# Revit family: RN 81167 Optipress-Aquaplus-Sicherheitsgarnitur
name_source: partatom
category: Rohrzubehör
units: mm (PartAtom-declared; Revit-internal decimal feet)

## family parameters
Arbeitsebenenbasiert = Nein
Beim Laden mit Abzugskörper schneiden = Nein
Bemaßung runder Anschluss = Durchmesser verwenden
Gemeinsam genutzt = Nein
Immer vertikal = Ja
Teiletyp = Ventil - Zerlegung in

## types (5) — shared parameters
1.010.00.2 Blattnummer der Richtlinie = 17
1.010.00.3 Ausgabedatum (Monat) der Richtlinie = 201601
1.010.00.4 Herstellername = R. Nussbaum AG
1.010.00.5 Revisionsdatum der Datei = 20190528
1.010.00.6 Webadresse des Herstellers = http://www.nussbaum.ch
1.100.00.3 Sortiernummer für Anzeigereihenfolge = 5
1.100.00.4 Produktbezeichnung = Sicherheitsarmaturen
1.960/3L.00.8 Link (URL) = https://www.nussbaum.ch
17.700.00.4 Armaturentyp = 6
17.700.00.7 Maximale Betriebstemperatur TB [°C] = 90
17.700.00.8 Maximaler Betriebsdruck (Arbeitsdruck) ps [1.0 · 105 Pa] = 16
Connector Visibility = Nein
EnclosingSpace Visibility = Nein

## per-type parameters (varying)
| type | 1.800.00.3 TGA-Nummer | 1.810.00.3 Hersteller-Bestellnummer | 1.810.00.4 DATANORM-Nummer | 1.810.00.5 StLB-Nummer | 1.810.00.6 GTIN-Nummer | 17.700.00.30 Produktbeschreibung | 17.700.00.5 Nennweite DN | 17.700.00.6 kvs-Wert [m3/h] | CONNECTOR0_DIAMETER_dZ_0r | CONNECTOR0_dZ_00 | CONNECTOR0_dZ_01 | CONNECTOR0_ref_dZ | CONNECTOR1_DIAMETER_dZ_0r | CONNECTOR1_dZ_00 | CONNECTOR1_dZ_01 | CONNECTOR1_ref_dZ | CONNECTOR2_DIAMETER_dZ_0r | CONNECTOR2_dZ_00 | CONNECTOR2_ref_dX | R. Nussbaum AG 81167.24 de Visibility | R. Nussbaum AG 81167.25 de Visibility | R. Nussbaum AG 81167.26 de Visibility | R. Nussbaum AG 81167.27 de Visibility | R. Nussbaum AG 81167.30 de Visibility |
| DN 20 | 0050180000000000000000000000020070000000000000000100000000 | 81167.24 | 81167.24 | 612.174 | 7612945737458 | 81167.24, Optipress-Aquaplus-Sicherheitsgarnitur, Sicherheitsventil 6 bar fest ei | 20 | 10.8 | 20 mm  [stored 0.0656168 ft] | 59 mm | 35 mm | 35 mm | 20 mm  [stored 0.0656168 ft] | 43 mm  [stored 0.141076 ft] | 67 mm | 43 mm  [stored 0.141076 ft] | 20 mm  [stored 0.0656168 ft] | 16 mm  [stored 0.0524934 ft] | 70 mm | Ja | Nein | Nein | Nein | Nein |
| DN 25 | 0050180000000000000000000000020070000000000000000200000000 | 81167.25 | 81167.25 | 612.175 | 7612945738219 | 81167.25, Optipress-Aquaplus-Sicherheitsgarnitur, Sicherheitsventil 6 bar fest ei | 25 | 16.8 | 25 mm  [stored 0.082021 ft] | 64 mm | 40 mm | 40 mm | 25 mm  [stored 0.082021 ft] | 47 mm | 71 mm | 47 mm | 20 mm  [stored 0.0656168 ft] | 15 mm  [stored 0.0492126 ft] | 75 mm | Nein | Ja | Nein | Nein | Nein |
| DN 32 | 0050180000000000000000000000020070000000000000000300000000 | 81167.26 | 81167.26 | 612.176 | 7612945735461 | 81167.26, Optipress-Aquaplus-Sicherheitsgarnitur, Sicherheitsventil 6 bar fest ei | 32 | 31.2 | 32 mm | 74 mm | 48 mm | 48 mm | 32 mm | 55 mm | 81 mm | 55 mm | 20 mm  [stored 0.0656168 ft] | 15 mm  [stored 0.0492126 ft] | 80 mm | Nein | Nein | Ja | Nein | Nein |
| DN 40 | 0050180000000000000000000000020070000000000000000400000000 | 81167.27 | 81167.27 | 612.177 | 7612945733856 | 81167.27, Optipress-Aquaplus-Sicherheitsgarnitur, Sicherheitsventil 6 bar fest ei | 40 | 45 | 40 mm | 88 mm | 52 mm | 52 mm | 40 mm | 61 mm | 97 mm | 61 mm | 25 mm  [stored 0.082021 ft] | 17 mm | 80 mm | Nein | Nein | Nein | Ja | Nein |
| DN 32 1 | 0050180000000000000000000000020070000000000000000500000000 | 81167.30 | 81167.30 |  | 7612945735478 | 81167.30, Optipress-Aquaplus-Sicherheitsgarnitur, Sicherheitsventil 6 bar fest ei | 32 | 31.2 | 32 mm | 73 mm | 47 mm | 47 mm | 32 mm | 56 mm | 82 mm | 56 mm | 25 mm  [stored 0.082021 ft] | 17 mm | 80 mm | Nein | Nein | Nein | Nein | Ja |

note: [stored X ft] marks values corroborated as IEEE doubles in the binary element streams (Revit-internal decimal feet)

## geometry (parser evidence)
native form markers: Sweep x3
no freeform markers — native parametric forms only
